# Revit family: Washroom-Accessories_Lotion-or-Soap-Dispenser-OneShot_Rubbermaid
name_source: partatom
category: Generic Models
units: mm (PartAtom-declared; Revit-internal decimal feet)

## family parameters
Can host rebar = No
Cut with Voids When Loaded = No
Host = Face
Maintain Annotation Orientation = No
Part Type = Normal
Room Calculation Point = No
Round Connector Dimension = Use Diameter
Shared = No

## types (8) — shared parameters
CAD Details = https://www.arcat.com
Default Elevation = 4' - 0"
Keynote = 11 82 00
Manufacturer = Rubbermaid Commercial
Product Page URL = https://www.arcat.com
Specification = https://www.arcat.com
URL = https://www.rubbermaidcommercial.com

## per-type parameters (varying)
| type | Body Material |
| FG401310_OneShot Lotion Dispenser | Rubbermaid_Polished Chrome/Black |
| FG402073_OneShot Lotion Dispenser | Rubbermaid_Polished Chrome |
| FG401528_OneShot Lotion Dispenser | Rubbermaid_Polished Chrome/Black |
| FG401832_OneShot Lotion Dispenser - Metal Spout | Rubbermaid_Polished Chrome/Black |
| FG402241_OneShot Lotion Dispenser - Low Profile | Rubbermaid_Polished Chrome |
| FG402243_OneShot Lotion Dispenser - Low Profile Metal | Rubbermaid_Polished Chrome |
| 1938171_OneShot Foam Dispenser - Low Profile | Rubbermaid_Polished Chrome |
| FG4870465_OneShot Foam Dispenser - Low Profile Metal | Rubbermaid_Polished Chrome |

## geometry (parser evidence)
native form markers: Sweep x2
no freeform markers — native parametric forms only
